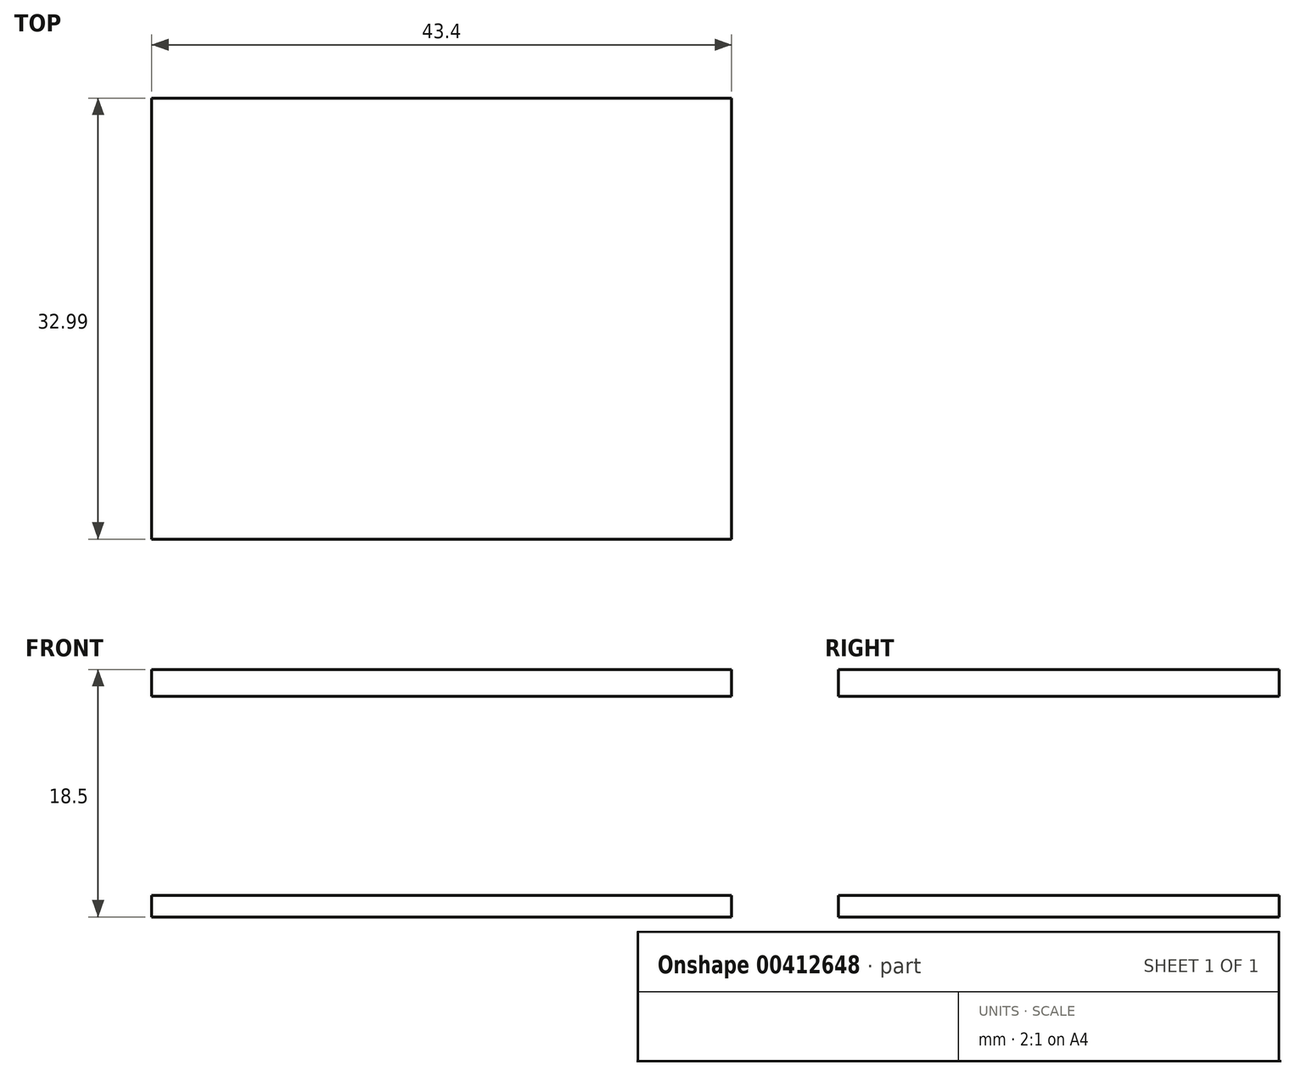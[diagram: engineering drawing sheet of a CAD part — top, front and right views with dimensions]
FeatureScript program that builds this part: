
annotation { "Feature Type Name" : "Feature", "Feature Type Description" : "" }
export const myFeature = defineFeature(function(context is Context, id is Id, definition is map)
    precondition{}
    {
        {
            var Q0;
            Q0=qCreatedBy(makeId("Top.planeOp"),FACE);
            var sketch = newSketch(context, id + "F0", { "sketchPlane" : qUnion([Q0])});
            skLineSegment(sketch, "E0.bottom", {"start": v(0, 0) * mm, "end": v(43.4, 0) * mm});
            skLineSegment(sketch, "E0.top", {"start": v(0, 32.99) * mm, "end": v(43.4, 32.99) * mm});
            skLineSegment(sketch, "E0.left", {"start": v(0, 0) * mm, "end": v(0, 32.99) * mm});
            skLineSegment(sketch, "E0.right", {"start": v(43.4, 0) * mm, "end": v(43.4, 32.99) * mm});
            skSolve(sketch);
        }
        {
            var Q0;
            Q0=qSketchRegion(id+"F0",true);
            extrude(context, id + "F1", {"entities" : qUnion([Q0]), "depth" : 2 * mm});
        }
        {
            var Q0;
            Q0=makeQuery(id+"F1.opExtrude","CAP_FACE",FACE,{"disambiguationData":[OSD([sQuery(id+"F0.wireOp",EDGE,"E0.bottom"),sQuery(id+"F0.wireOp",EDGE,"E0.top"),sQuery(id+"F0.wireOp",EDGE,"E0.left"),sQuery(id+"F0.wireOp",EDGE,"E0.right")])],"isStart":true});
            var sketch = newSketch(context, id + "F2", { "sketchPlane" : qUnion([Q0])});
            skLineSegment(sketch, "E1.bottom", {"start": v(0, 0) * mm, "end": v(43.4, 0) * mm});
            skLineSegment(sketch, "E1.top", {"start": v(0, -32.99) * mm, "end": v(43.4, -32.99) * mm});
            skLineSegment(sketch, "E1.left", {"start": v(0, 0) * mm, "end": v(0, -32.99) * mm});
            skLineSegment(sketch, "E1.right", {"start": v(43.4, 0) * mm, "end": v(43.4, -32.99) * mm});
            skSolve(sketch);
        }
        {
            var Q0;
            Q0=qSketchRegion(id+"F2",true);
            extrude(context, id + "F3", {"entities" : qUnion([Q0]), "operationType" : NewBodyOperationType.ADD, "depth" : 16.5 * mm});
        }
        {
            var Q0;
            Q0=makeQuery(id+"F3.boolean.opBoolean","MERGE",FACE,{"derivedFrom":[makeQuery(id+"F1.opExtrude","SWEPT_FACE",FACE,{"disambiguationData":[OSD([sQuery(id+"F0.wireOp",EDGE,"E0.bottom")])]}),makeQuery(id+"F3.opExtrude","SWEPT_FACE",FACE,{"disambiguationData":[OSD([sQuery(id+"F2.wireOp",EDGE,"E1.bottom")])]})]});
            var sketch = newSketch(context, id + "F4", { "sketchPlane" : qUnion([Q0])});
            skLineSegment(sketch, "E2.bottom", {"start": v(0, 0) * mm, "end": v(43.4, 0) * mm});
            skLineSegment(sketch, "E2.top", {"start": v(0, -14.9) * mm, "end": v(43.4, -14.9) * mm});
            skLineSegment(sketch, "E2.left", {"start": v(0, 0) * mm, "end": v(0, -14.9) * mm});
            skLineSegment(sketch, "E2.right", {"start": v(43.4, 0) * mm, "end": v(43.4, -14.9) * mm});
            skSolve(sketch);
        }
        {
            var Q0;
            Q0=qSketchRegion(id+"F4",true);
            extrude(context, id + "F5", {"entities" : qUnion([Q0]), "operationType" : NewBodyOperationType.REMOVE, "oppositeDirection" : true, "depth" : 35 * mm});
        }
    });
